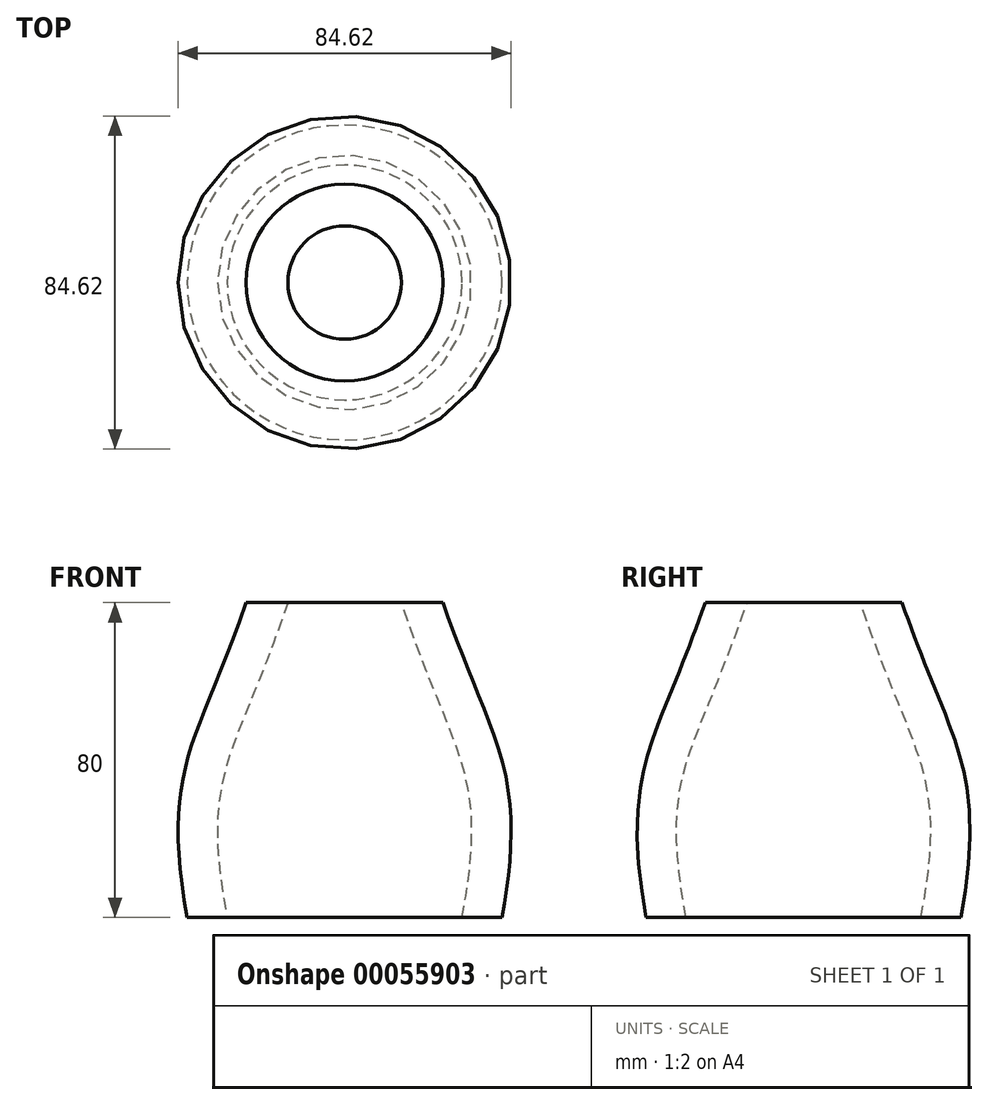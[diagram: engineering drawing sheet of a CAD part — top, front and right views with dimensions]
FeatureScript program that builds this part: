
annotation { "Feature Type Name" : "Feature", "Feature Type Description" : "" }
export const myFeature = defineFeature(function(context is Context, id is Id, definition is map)
    precondition{}
    {
        {
            var Q0;
            Q0=qCreatedBy(makeId("Front.planeOp"),FACE);
            var sketch = newSketch(context, id + "F0", { "sketchPlane" : qUnion([Q0])});
            skLineSegment(sketch, "E0", {"start": v(0, 0) * mm, "end": v(0, 80) * mm});
            skLineSegment(sketch, "E1", {"start": v(0, 80) * mm, "end": v(25, 80) * mm});
            skLineSegment(sketch, "E2", {"start": v(0, 0) * mm, "end": v(40, 0) * mm});
            skFitSpline(sketch, "E3", {"points": [v(25, 80) * mm, v(40.39, 38.36) * mm, v(40, 0) * mm], "startDerivative": vector(40.38, -115.45) * mm, "endDerivative": vector(-19.03, -103.4) * mm});
            skSolve(sketch);
        }
        {
            var Q0;
            Q0=makeQuery(id+"F0.imprint","IMPRINT",FACE,{"disambiguationData":[TD([[makeQuery(id+"F0.imprint","IMPRINT",EDGE,{"derivedFrom":sQuery(id+"F0.wireOp",EDGE,"E0")}),-1.0]])]});
            var Q1;
            Q1=sQuery(id+"F0.wireOp",EDGE,"E0");
            revolve(context, id + "F1", {"entities" : qUnion([Q0]), "axis" : qUnion([Q1]), "revolveType" : RevolveType.FULL});
        }
        {
            var Q0;
            Q0=makeQuery(id+"F1.opRevolve","SWEPT_FACE",FACE,{"disambiguationData":[OSD([sQuery(id+"F0.wireOp",EDGE,"E2")])]});
            var Q1;
            Q1=makeQuery(id+"F1.opRevolve","SWEPT_FACE",FACE,{"disambiguationData":[OSD([sQuery(id+"F0.wireOp",EDGE,"E1")])]});
            shell(context, id + "F2", {"entities" : qUnion([Q0, Q1]), "thickness" : 10 * mm});
        }
    });
